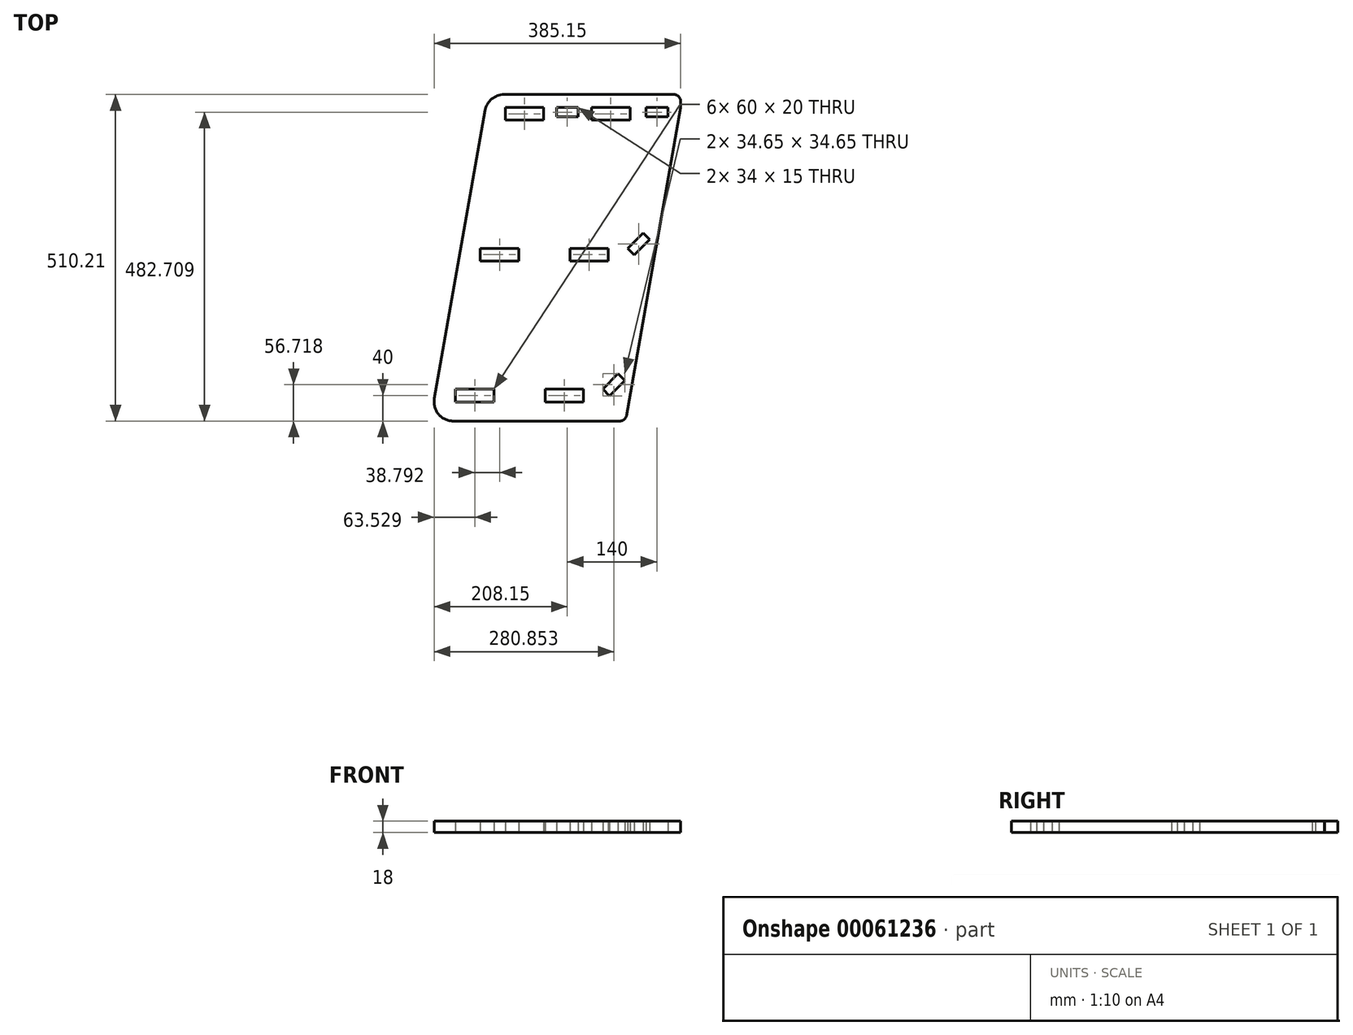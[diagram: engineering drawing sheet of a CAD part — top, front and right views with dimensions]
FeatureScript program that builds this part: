
annotation { "Feature Type Name" : "Feature", "Feature Type Description" : "" }
export const myFeature = defineFeature(function(context is Context, id is Id, definition is map)
    precondition{}
    {
        {
            var Q0;
            Q0=qCreatedBy(makeId("Top.planeOp"),FACE);
            var sketch = newSketch(context, id + "F0", { "sketchPlane" : qUnion([Q0])});
            skLineSegment(sketch, "E0.top", {"start": v(0, 0) * mm, "end": v(314.58, -55.47) * mm});
            skLineSegment(sketch, "E0.left", {"start": v(85.6, 485.42) * mm, "end": v(6.2, 35.2) * mm});
            skLineSegment(sketch, "E0.right", {"start": v(395.19, 513.58) * mm, "end": v(306.09, 8.26) * mm});
            skLineSegment(sketch, "E1", {"start": v(35.75, 0) * mm, "end": v(296.24, 0) * mm});
            skPoint(sketch, "E2", {"position": v(374.32, 0) * mm});
            skLineSegment(sketch, "E3", {"start": v(380.9, 510.2) * mm, "end": v(115.14, 510.2) * mm});
            skLineSegment(sketch, "E4.bottom", {"start": v(39.28, 30) * mm, "end": v(99.28, 30) * mm});
            skLineSegment(sketch, "E4.top", {"start": v(39.28, 50) * mm, "end": v(99.28, 50) * mm});
            skLineSegment(sketch, "E4.left", {"start": v(39.28, 30) * mm, "end": v(39.28, 50) * mm});
            skLineSegment(sketch, "E4.right", {"start": v(99.28, 30) * mm, "end": v(99.28, 50) * mm});
            skLineSegment(sketch, "E5.1.0.0", {"start": v(239.28, 30) * mm, "end": v(239.28, 50) * mm});
            skLineSegment(sketch, "E5.1.0.1", {"start": v(179.28, 30) * mm, "end": v(179.28, 50) * mm});
            skLineSegment(sketch, "E5.1.0.2", {"start": v(179.28, 30) * mm, "end": v(239.28, 30) * mm});
            skLineSegment(sketch, "E5.1.0.3", {"start": v(179.28, 50) * mm, "end": v(239.28, 50) * mm});
            skLineSegment(sketch, "E5.direction1", {"start": v(99.28, 30) * mm, "end": v(239.28, 30) * mm, "construction": true});
            skLineSegment(sketch, "E6.bottom", {"start": v(269.28, 50) * mm, "end": v(293.32, 74.04) * mm});
            skLineSegment(sketch, "E6.top", {"start": v(279.89, 39.4) * mm, "end": v(303.93, 63.44) * mm});
            skLineSegment(sketch, "E6.left", {"start": v(269.28, 50) * mm, "end": v(279.89, 39.4) * mm});
            skLineSegment(sketch, "E6.right", {"start": v(293.32, 74.04) * mm, "end": v(303.93, 63.44) * mm});
            skLineSegment(sketch, "E7", {"start": v(239.28, 50) * mm, "end": v(439.66, 50) * mm});
            skLineSegment(sketch, "E8.bottom", {"start": v(78.07, 250) * mm, "end": v(138.07, 250) * mm});
            skLineSegment(sketch, "E9.1.0.0", {"start": v(278.07, 250) * mm, "end": v(278.07, 270) * mm});
            skLineSegment(sketch, "E9.1.0.3", {"start": v(218.07, 270) * mm, "end": v(278.07, 270) * mm});
            skLineSegment(sketch, "E9.1.0.2", {"start": v(218.07, 250) * mm, "end": v(278.07, 250) * mm});
            skLineSegment(sketch, "E8.right", {"start": v(138.07, 250) * mm, "end": v(138.07, 270) * mm});
            skLineSegment(sketch, "E8.left", {"start": v(78.07, 250) * mm, "end": v(78.07, 270) * mm});
            skLineSegment(sketch, "E10.bottom", {"start": v(308.07, 270) * mm, "end": v(332.11, 294.04) * mm});
            skLineSegment(sketch, "E8.top", {"start": v(78.07, 270) * mm, "end": v(138.07, 270) * mm});
            skLineSegment(sketch, "E11", {"start": v(278.07, 270) * mm, "end": v(756.24, 270) * mm});
            skLineSegment(sketch, "E9.direction1", {"start": v(138.07, 250) * mm, "end": v(278.07, 250) * mm, "construction": true});
            skLineSegment(sketch, "E10.top", {"start": v(318.68, 259.4) * mm, "end": v(342.72, 283.44) * mm});
            skLineSegment(sketch, "E9.1.0.1", {"start": v(218.07, 250) * mm, "end": v(218.07, 270) * mm});
            skLineSegment(sketch, "E10.left", {"start": v(308.07, 270) * mm, "end": v(318.68, 259.4) * mm});
            skLineSegment(sketch, "E10.right", {"start": v(332.11, 294.04) * mm, "end": v(342.72, 283.44) * mm});
            skLineSegment(sketch, "E12.bottom", {"start": v(116.9, 470.2) * mm, "end": v(176.9, 470.2) * mm});
            skLineSegment(sketch, "E13.1.0.0", {"start": v(311.9, 470.2) * mm, "end": v(311.9, 490.2) * mm});
            skLineSegment(sketch, "E13.1.0.3", {"start": v(251.9, 490.2) * mm, "end": v(311.9, 490.2) * mm});
            skLineSegment(sketch, "E13.1.0.2", {"start": v(251.9, 470.2) * mm, "end": v(311.9, 470.2) * mm});
            skLineSegment(sketch, "E12.right", {"start": v(176.9, 470.2) * mm, "end": v(176.9, 490.2) * mm});
            skLineSegment(sketch, "E12.left", {"start": v(116.9, 470.2) * mm, "end": v(116.9, 490.2) * mm});
            skLineSegment(sketch, "E12.top", {"start": v(116.9, 490.2) * mm, "end": v(176.9, 490.2) * mm});
            skLineSegment(sketch, "E13.direction1", {"start": v(176.9, 470.2) * mm, "end": v(311.9, 470.2) * mm, "construction": true});
            skLineSegment(sketch, "E13.1.0.1", {"start": v(251.9, 470.2) * mm, "end": v(251.9, 490.2) * mm});
            skLineSegment(sketch, "E14.1.0.0", {"start": v(370.9, 475.2) * mm, "end": v(370.9, 490.2) * mm});
            skLineSegment(sketch, "E15.bottom", {"start": v(196.9, 475.2) * mm, "end": v(230.9, 475.2) * mm});
            skLineSegment(sketch, "E14.1.0.1", {"start": v(336.9, 475.2) * mm, "end": v(336.9, 490.2) * mm});
            skLineSegment(sketch, "E15.right", {"start": v(230.9, 475.2) * mm, "end": v(230.9, 490.2) * mm});
            skLineSegment(sketch, "E14.direction1", {"start": v(230.9, 475.2) * mm, "end": v(370.9, 475.2) * mm, "construction": true});
            skLineSegment(sketch, "E15.left", {"start": v(196.9, 475.2) * mm, "end": v(196.9, 490.2) * mm});
            skLineSegment(sketch, "E14.1.0.3", {"start": v(336.9, 490.2) * mm, "end": v(370.9, 490.2) * mm});
            skLineSegment(sketch, "E15.top", {"start": v(196.9, 490.2) * mm, "end": v(230.9, 490.2) * mm});
            skLineSegment(sketch, "E14.1.0.2", {"start": v(336.9, 475.2) * mm, "end": v(370.9, 475.2) * mm});
            skPoint(sketch, "E16.newPointA", {"position": v(95.5, 541.64) * mm});
            skArc(sketch, "E16.filletArc", {"start": v(115.14, 510.2) * mm, "mid": v(95.85, 503.19) * mm, "end": v(85.6, 485.42) * mm});
            skPoint(sketch, "E17.visualSharp", {"position": v(0, 0) * mm});
            skArc(sketch, "E17.filletArc", {"start": v(6.2, 35.2) * mm, "mid": v(12.77, 10.72) * mm, "end": v(35.75, 0) * mm});
            skLineSegment(sketch, "E18", {"start": v(390.9, 500.2) * mm, "end": v(390.9, 489.27) * mm});
            skArc(sketch, "E19.filletArc", {"start": v(390.9, 500.2) * mm, "mid": v(387.97, 507.28) * mm, "end": v(380.9, 510.2) * mm});
            skArc(sketch, "E20.filletArc", {"start": v(296.24, 0) * mm, "mid": v(302.66, 2.34) * mm, "end": v(306.09, 8.26) * mm});
            skSolve(sketch);
        }
        {
            var Q0;
            Q0 = qSketchRegion(id + "F0", true);
            extrude(context, id + "F1", {"entities" : qUnion([Q0]), "depth" : 18 * mm});
        }
    });
